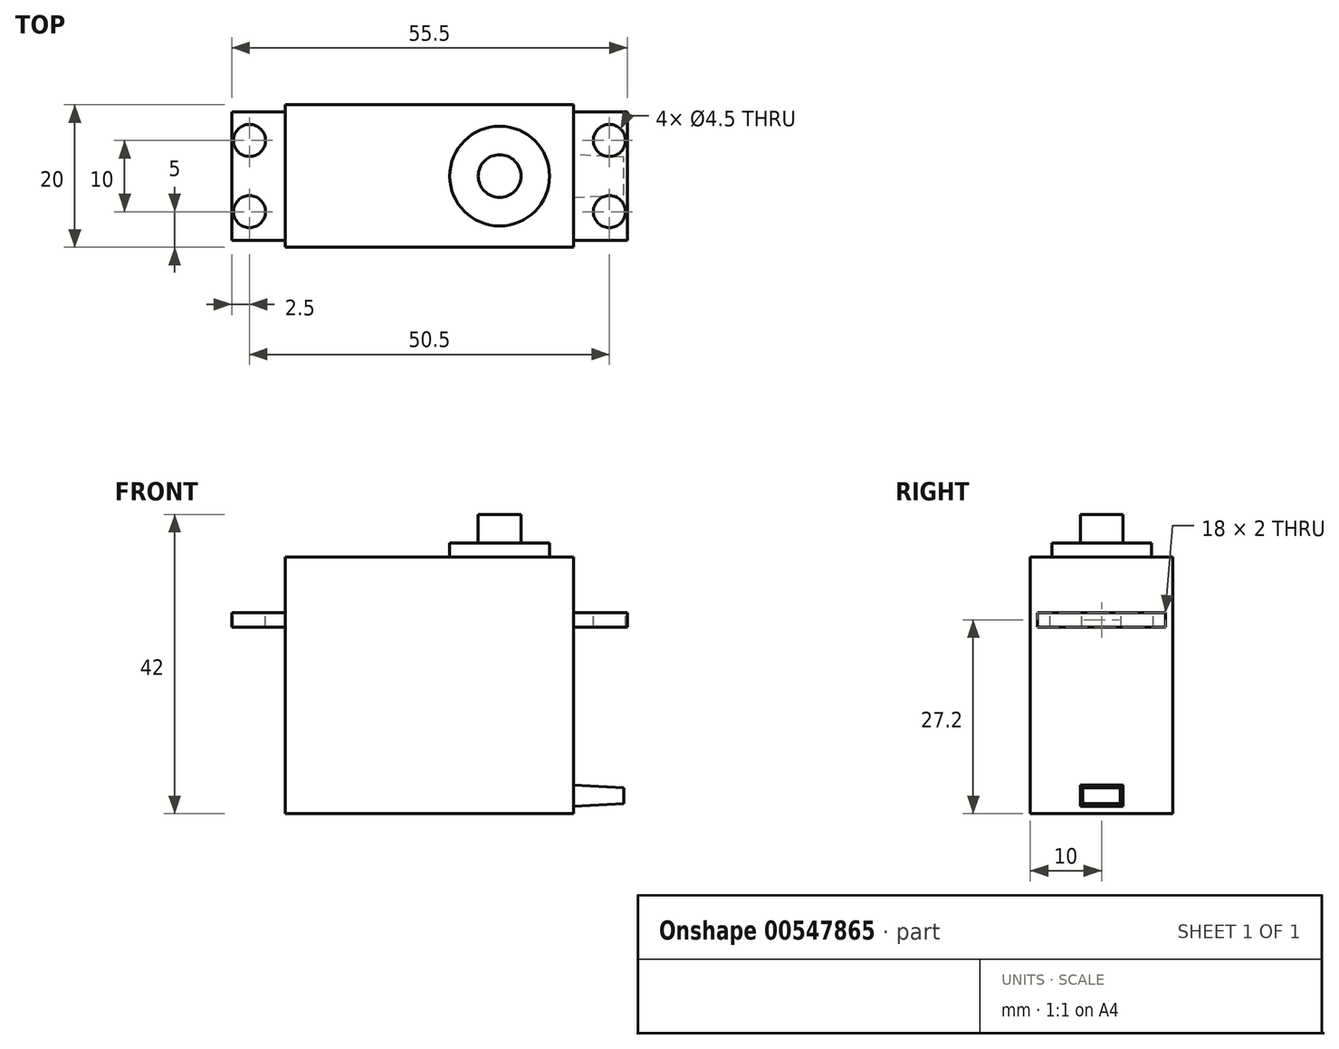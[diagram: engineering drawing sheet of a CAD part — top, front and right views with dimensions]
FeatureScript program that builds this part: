
annotation { "Feature Type Name" : "Feature", "Feature Type Description" : "" }
export const myFeature = defineFeature(function(context is Context, id is Id, definition is map)
    precondition{}
    {
        {
            var Q0;
            Q0=qCreatedBy(makeId("Top.planeOp"),FACE);
            var sketch = newSketch(context, id + "F0", { "sketchPlane" : qUnion([Q0])});
            skLineSegment(sketch, "E0.bottom", {"start": v(-40.5, 0) * mm, "end": v(0, 0) * mm});
            skLineSegment(sketch, "E0.top", {"start": v(-40.5, -20) * mm, "end": v(0, -20) * mm});
            skLineSegment(sketch, "E0.left", {"start": v(-40.5, 0) * mm, "end": v(-40.5, -20) * mm});
            skLineSegment(sketch, "E0.right", {"start": v(0, 0) * mm, "end": v(0, -20) * mm});
            skSolve(sketch);
        }
        {
            var Q0;
            Q0=makeQuery(id+"F0.imprint","IMPRINT",FACE,{"disambiguationData":[TD([[makeQuery(id+"F0.imprint","IMPRINT",EDGE,{"derivedFrom":sQuery(id+"F0.wireOp",EDGE,"E0.bottom")}),-1.0]])]});
            extrude(context, id + "F1", {"entities" : qUnion([Q0]), "depth" : 36 * mm, "offsetDistance" : 25 * mm});
        }
        {
            var Q0;
            Q0=makeQuery(id+"F1.opExtrude","CAP_FACE",FACE,{"disambiguationData":[OSD([sQuery(id+"F0.wireOp",EDGE,"E0.bottom"),sQuery(id+"F0.wireOp",EDGE,"E0.top"),sQuery(id+"F0.wireOp",EDGE,"E0.left"),sQuery(id+"F0.wireOp",EDGE,"E0.right")])],"isStart":false});
            var sketch = newSketch(context, id + "F2", { "sketchPlane" : qUnion([Q0])});
            skCircle(sketch, "E1", {"center": v(-10.4, -10) * mm, "radius": 7 * mm});
            skPoint(sketch, "E1.centerSnap0", {"position": v(0, -10) * mm});
            skLineSegment(sketch, "E2", {"start": v(-10.4, -10) * mm, "end": v(0, -10) * mm, "construction": true});
            skSolve(sketch);
        }
        {
            var Q0;
            Q0=makeQuery(id+"F2.imprint","IMPRINT",FACE,{"disambiguationData":[TD([[makeQuery(id+"F2.imprint","IMPRINT",EDGE,{"derivedFrom":sQuery(id+"F2.wireOp",EDGE,"E1")}),1.0]])]});
            extrude(context, id + "F3", {"entities" : qUnion([Q0]), "operationType" : NewBodyOperationType.ADD, "depth" : 2 * mm, "offsetDistance" : 25 * mm});
        }
        {
            var Q0;
            Q0=makeQuery(id+"F3.opExtrude","CAP_FACE",FACE,{"disambiguationData":[OSD([sQuery(id+"F2.wireOp",EDGE,"E1")])],"isStart":false});
            var sketch = newSketch(context, id + "F4", { "sketchPlane" : qUnion([Q0])});
            skCircle(sketch, "E3", {"center": v(-10.4, -10) * mm, "radius": 3 * mm});
            skSolve(sketch);
        }
        {
            var Q0;
            Q0=makeQuery(id+"F4.imprint","IMPRINT",FACE,{"disambiguationData":[TD([[makeQuery(id+"F4.imprint","IMPRINT",EDGE,{"derivedFrom":sQuery(id+"F4.wireOp",EDGE,"E3")}),1.0]])]});
            extrude(context, id + "F5", {"entities" : qUnion([Q0]), "operationType" : NewBodyOperationType.ADD, "depth" : 4 * mm, "offsetDistance" : 25 * mm});
        }
        {
            var Q0;
            Q0=makeQuery(id+"F1.opExtrude","SWEPT_FACE",FACE,{"disambiguationData":[OSD([sQuery(id+"F0.wireOp",EDGE,"E0.right")])]});
            var sketch = newSketch(context, id + "F6", { "sketchPlane" : qUnion([Q0])});
            skLineSegment(sketch, "E4.bottom", {"start": v(-19, 28.2) * mm, "end": v(-1, 28.2) * mm});
            skLineSegment(sketch, "E4.top", {"start": v(-19, 26.2) * mm, "end": v(-1, 26.2) * mm});
            skLineSegment(sketch, "E4.left", {"start": v(-19, 28.2) * mm, "end": v(-19, 26.2) * mm});
            skLineSegment(sketch, "E4.right", {"start": v(-1, 28.2) * mm, "end": v(-1, 26.2) * mm});
            skSolve(sketch);
        }
        {
            var Q0;
            Q0=makeQuery(id+"F6.imprint","IMPRINT",FACE,{"disambiguationData":[TD([[makeQuery(id+"F6.imprint","IMPRINT",EDGE,{"derivedFrom":sQuery(id+"F6.wireOp",EDGE,"E4.bottom")}),-1.0]])]});
            extrude(context, id + "F7", {"entities" : qUnion([Q0]), "operationType" : NewBodyOperationType.ADD, "depth" : 7.5 * mm, "offsetDistance" : 25 * mm});
        }
        {
            var Q0;
            Q0=makeQuery(id+"F1.opExtrude","SWEPT_FACE",FACE,{"disambiguationData":[OSD([sQuery(id+"F0.wireOp",EDGE,"E0.left")])]});
            var sketch = newSketch(context, id + "F8", { "sketchPlane" : qUnion([Q0])});
            skLineSegment(sketch, "E5.bottom", {"start": v(1, 28.2) * mm, "end": v(19, 28.2) * mm});
            skLineSegment(sketch, "E5.top", {"start": v(1, 26.2) * mm, "end": v(19, 26.2) * mm});
            skLineSegment(sketch, "E5.left", {"start": v(1, 28.2) * mm, "end": v(1, 26.2) * mm});
            skLineSegment(sketch, "E5.right", {"start": v(19, 28.2) * mm, "end": v(19, 26.2) * mm});
            skSolve(sketch);
        }
        {
            var Q0;
            Q0=makeQuery(id+"F8.imprint","IMPRINT",FACE,{"disambiguationData":[TD([[makeQuery(id+"F8.imprint","IMPRINT",EDGE,{"derivedFrom":sQuery(id+"F8.wireOp",EDGE,"E5.bottom")}),-1.0]])]});
            extrude(context, id + "F9", {"entities" : qUnion([Q0]), "operationType" : NewBodyOperationType.ADD, "depth" : 7.5 * mm, "offsetDistance" : 25 * mm});
        }
        {
            var Q0;
            Q0=makeQuery(id+"F9.opExtrude","SWEPT_FACE",FACE,{"disambiguationData":[OSD([sQuery(id+"F8.wireOp",EDGE,"E5.bottom")])]});
            var sketch = newSketch(context, id + "F10", { "sketchPlane" : qUnion([Q0])});
            skCircle(sketch, "E6", {"center": v(5, -15) * mm, "radius": 2.25 * mm});
            skCircle(sketch, "E7", {"center": v(5, -5) * mm, "radius": 2.25 * mm});
            skLineSegment(sketch, "E8", {"start": v(5, -15) * mm, "end": v(5, -5) * mm, "construction": true});
            skLineSegment(sketch, "E9", {"start": v(5, -10) * mm, "end": v(7.5, -10) * mm, "construction": true});
            skLineSegment(sketch, "E10", {"start": v(-48, -1) * mm, "end": v(7.5, -1) * mm, "construction": true});
            skLineSegment(sketch, "E11", {"start": v(-20.25, -1) * mm, "end": v(-20.25, -23.42) * mm, "construction": true});
            skCircle(sketch, "E12.MirrorC", {"center": v(-45.5, -5) * mm, "radius": 2.25 * mm});
            skCircle(sketch, "E13.MirrorC", {"center": v(-45.5, -15) * mm, "radius": 2.25 * mm});
            skSolve(sketch);
        }
        {
            var Q0;
            Q0 = qSketchRegion(id + "F10", true);
            extrude(context, id + "F11", {"entities" : qUnion([Q0]), "operationType" : NewBodyOperationType.REMOVE, "oppositeDirection" : true, "depth" : 25 * mm, "offsetDistance" : 25 * mm});
        }
        {
            var Q0;
            Q0=makeQuery(id+"F1.opExtrude","SWEPT_FACE",FACE,{"disambiguationData":[OSD([sQuery(id+"F0.wireOp",EDGE,"E0.right")])]});
            var sketch = newSketch(context, id + "F12", { "sketchPlane" : qUnion([Q0])});
            skLineSegment(sketch, "E14.bottom", {"start": v(-13, 4.03) * mm, "end": v(-7, 4.03) * mm});
            skLineSegment(sketch, "E14.top", {"start": v(-13, 1.03) * mm, "end": v(-7, 1.03) * mm});
            skLineSegment(sketch, "E14.left", {"start": v(-13, 4.03) * mm, "end": v(-13, 1.03) * mm});
            skLineSegment(sketch, "E14.right", {"start": v(-7, 4.03) * mm, "end": v(-7, 1.03) * mm});
            skLineSegment(sketch, "E15", {"start": v(-10, 4.03) * mm, "end": v(-10, 0) * mm, "construction": true});
            skSolve(sketch);
        }
        {
            var Q0;
            Q0=makeQuery(id+"F12.imprint","IMPRINT",FACE,{"disambiguationData":[TD([[makeQuery(id+"F12.imprint","IMPRINT",EDGE,{"derivedFrom":sQuery(id+"F12.wireOp",EDGE,"E14.bottom")}),-1.0]])]});
            extrude(context, id + "F13", {"entities" : qUnion([Q0]), "operationType" : NewBodyOperationType.ADD, "depth" : 7 * mm, "offsetDistance" : 25 * mm, "hasDraft" : true, "draftAngle" : 3 * degree, "draftPullDirection" : true});
        }
    });
